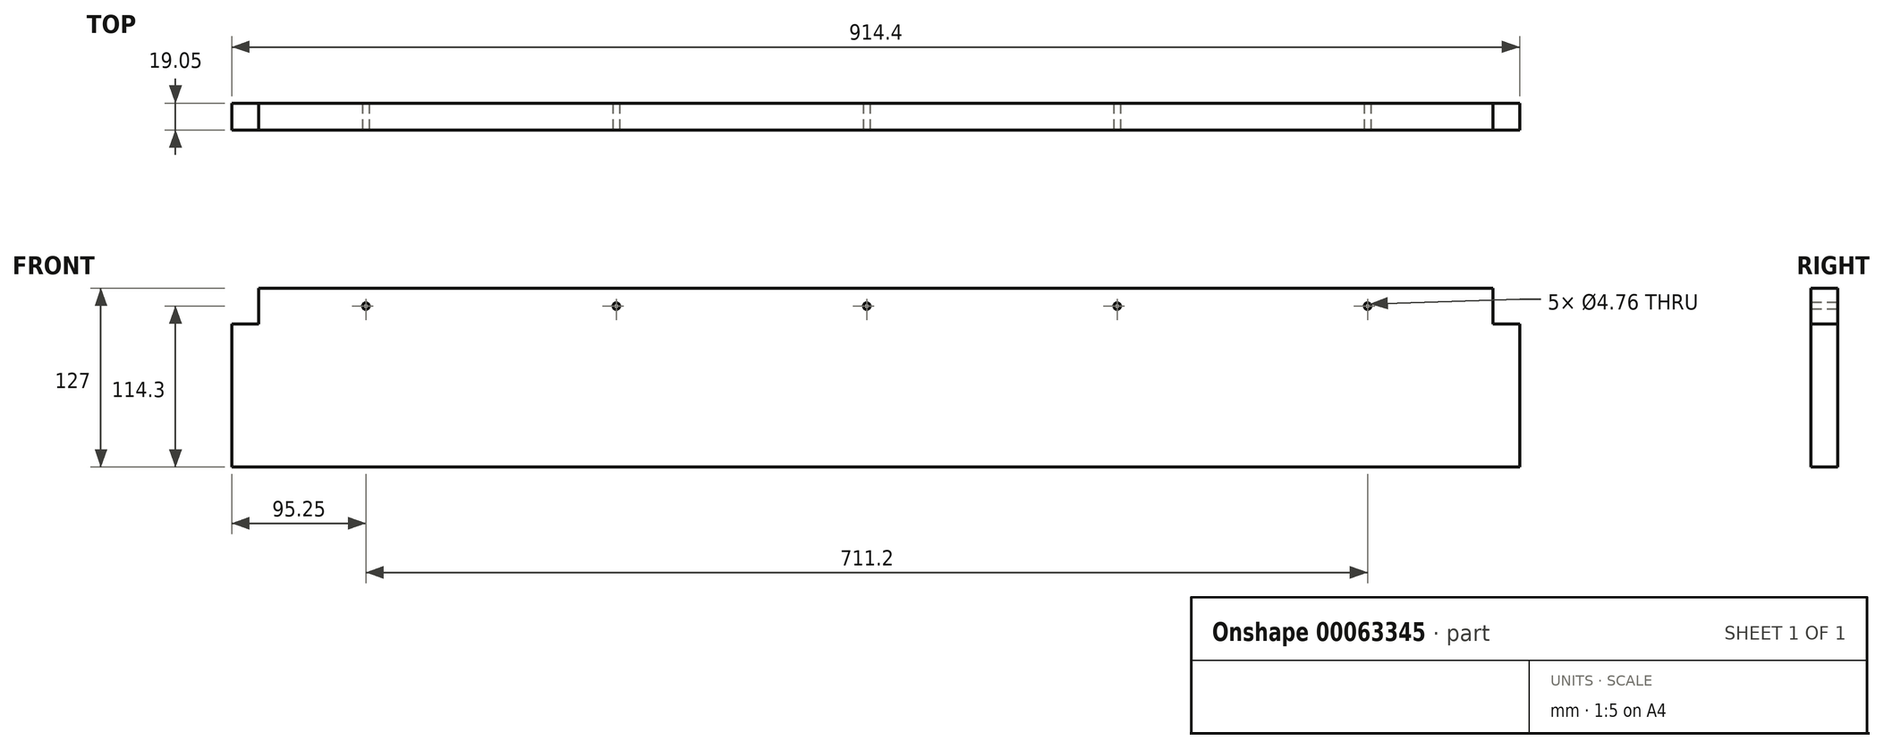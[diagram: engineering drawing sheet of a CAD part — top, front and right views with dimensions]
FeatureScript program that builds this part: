
annotation { "Feature Type Name" : "Feature", "Feature Type Description" : "" }
export const myFeature = defineFeature(function(context is Context, id is Id, definition is map)
    precondition{}
    {
        {
            var Q0;
            Q0=qCreatedBy(makeId("Front.planeOp"),FACE);
            var sketch = newSketch(context, id + "F0", { "sketchPlane" : qUnion([Q0])});
            skLineSegment(sketch, "E0.rect.bottom", {"start": v(457.2, -63.5) * mm, "end": v(-457.2, -63.5) * mm});
            skLineSegment(sketch, "E0.rect.top", {"start": v(457.2, 63.5) * mm, "end": v(-457.2, 63.5) * mm});
            skLineSegment(sketch, "E0.rect.left", {"start": v(457.2, -63.5) * mm, "end": v(457.2, 63.5) * mm});
            skLineSegment(sketch, "E0.rect.right", {"start": v(-457.2, -63.5) * mm, "end": v(-457.2, 63.5) * mm});
            skPoint(sketch, "E0.rect.middle", {"position": v(0, 0) * mm});
            skSolve(sketch);
        }
        {
            var Q0;
            Q0 = qSketchRegion(id + "F0", true);
            extrude(context, id + "F1", {"entities" : qUnion([Q0]), "oppositeDirection" : true, "depth" : 19.05 * mm});
        }
        {
            var Q0;
            Q0=makeQuery(id+"F1.opExtrude","CAP_FACE",FACE,{"disambiguationData":[OSD([sQuery(id+"F0.wireOp",EDGE,"E0.rect.bottom"),sQuery(id+"F0.wireOp",EDGE,"E0.rect.top"),sQuery(id+"F0.wireOp",EDGE,"E0.rect.left"),sQuery(id+"F0.wireOp",EDGE,"E0.rect.right")])],"isStart":true});
            var sketch = newSketch(context, id + "F2", { "sketchPlane" : qUnion([Q0])});
            skLineSegment(sketch, "E1.bottom", {"start": v(-457.2, 63.5) * mm, "end": v(-438.15, 63.5) * mm});
            skLineSegment(sketch, "E1.top", {"start": v(-457.2, 38.1) * mm, "end": v(-438.15, 38.1) * mm});
            skLineSegment(sketch, "E1.left", {"start": v(-457.2, 63.5) * mm, "end": v(-457.2, 38.1) * mm});
            skLineSegment(sketch, "E1.right", {"start": v(-438.15, 63.5) * mm, "end": v(-438.15, 38.1) * mm});
            skLineSegment(sketch, "E2.MirrorCS", {"start": v(457.2, 63.5) * mm, "end": v(457.2, 38.1) * mm});
            skLineSegment(sketch, "E3.MirrorCS", {"start": v(457.2, 63.5) * mm, "end": v(438.15, 63.5) * mm});
            skLineSegment(sketch, "E4.MirrorCS", {"start": v(438.15, 63.5) * mm, "end": v(438.15, 38.1) * mm});
            skLineSegment(sketch, "E5.MirrorCS", {"start": v(457.2, 38.1) * mm, "end": v(438.15, 38.1) * mm});
            skSolve(sketch);
        }
        {
            var Q0;
            Q0 = qSketchRegion(id + "F2", true);
            extrude(context, id + "F3", {"entities" : qUnion([Q0]), "operationType" : NewBodyOperationType.REMOVE, "endBound" : BoundingType.THROUGH_ALL, "oppositeDirection" : true, "depth" : 25.4 * mm});
        }
        {
            var Q0;
            Q0=makeQuery(id+"F1.opExtrude","CAP_FACE",FACE,{"disambiguationData":[OSD([sQuery(id+"F0.wireOp",EDGE,"E0.rect.bottom"),sQuery(id+"F0.wireOp",EDGE,"E0.rect.top"),sQuery(id+"F0.wireOp",EDGE,"E0.rect.left"),sQuery(id+"F0.wireOp",EDGE,"E0.rect.right")])],"isStart":true});
            var sketch = newSketch(context, id + "F4", { "sketchPlane" : qUnion([Q0])});
            skPoint(sketch, "E6", {"position": v(-361.95, 50.8) * mm});
            skPoint(sketch, "E7", {"position": v(-184.15, 50.8) * mm});
            skPoint(sketch, "E8", {"position": v(-6.35, 50.8) * mm});
            skPoint(sketch, "E9", {"position": v(171.45, 50.8) * mm});
            skPoint(sketch, "E10", {"position": v(349.25, 50.8) * mm});
            skSolve(sketch);
        }
        {
            var Q0;
            Q0=sQuery(id+"F4.wireOp",VERTEX,"E6");
            var Q1;
            Q1=sQuery(id+"F4.wireOp",VERTEX,"E7");
            var Q2;
            Q2=sQuery(id+"F4.wireOp",VERTEX,"E8");
            var Q3;
            Q3=sQuery(id+"F4.wireOp",VERTEX,"E9");
            var Q4;
            Q4=sQuery(id+"F4.wireOp",VERTEX,"E10");
            var Q5;
            Q5=makeQuery(id+"F1.opExtrude","SWEPT_BODY",BODY,{"disambiguationData":[OSD([sQuery(id+"F0.wireOp",EDGE,"E0.rect.bottom"),sQuery(id+"F0.wireOp",EDGE,"E0.rect.top"),sQuery(id+"F0.wireOp",EDGE,"E0.rect.left"),sQuery(id+"F0.wireOp",EDGE,"E0.rect.right")])]});
            hole(context, id + "F5", {"style" : HoleStyle.SIMPLE, "holeDiameter" : 4.76 * mm, "endStyle" : HoleEndStyle.THROUGH, "locations" : qUnion([Q0, Q1, Q2, Q3, Q4]), "scope" : qUnion([Q5])});
        }
    });
